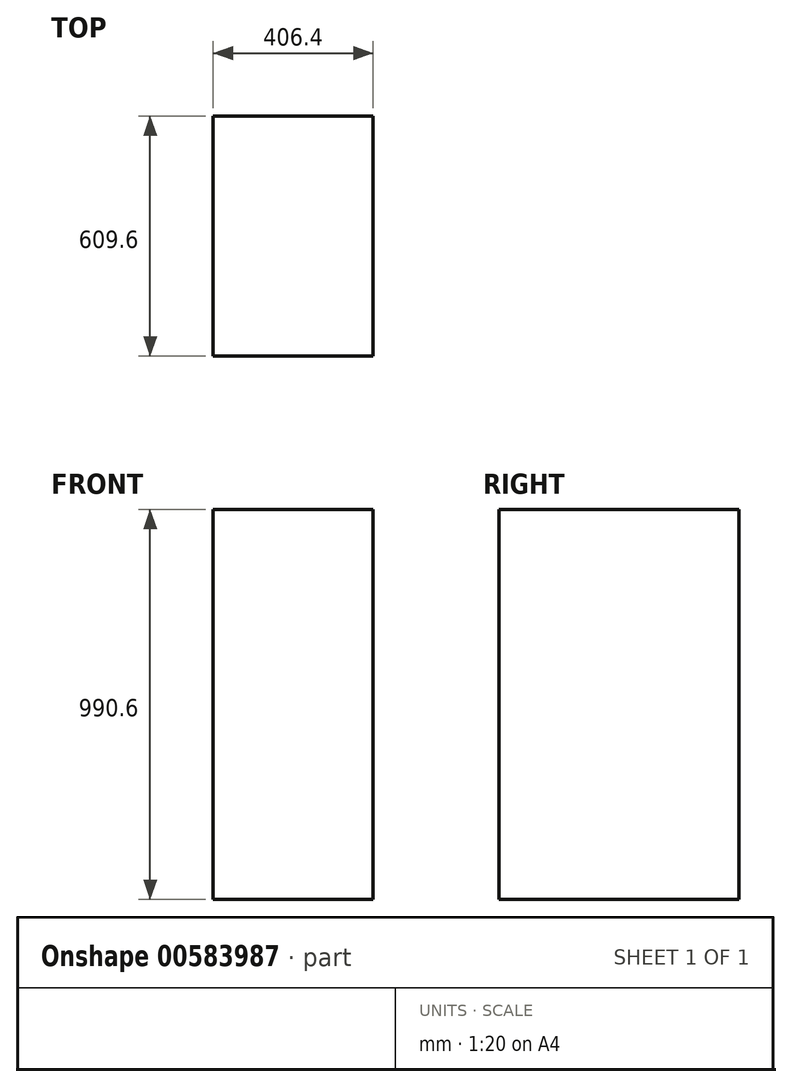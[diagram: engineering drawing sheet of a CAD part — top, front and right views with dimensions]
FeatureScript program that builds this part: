
annotation { "Feature Type Name" : "Feature", "Feature Type Description" : "" }
export const myFeature = defineFeature(function(context is Context, id is Id, definition is map)
    precondition{}
    {
        {
            var Q0;
            Q0=qCreatedBy(makeId("Top.planeOp"),FACE);
            var sketch = newSketch(context, id + "F0", { "sketchPlane" : qUnion([Q0])});
            skLineSegment(sketch, "E0.bottom", {"start": v(-202.1, 475.08) * mm, "end": v(204.3, 475.08) * mm});
            skLineSegment(sketch, "E0.top", {"start": v(-202.1, -134.52) * mm, "end": v(204.3, -134.52) * mm});
            skLineSegment(sketch, "E0.left", {"start": v(-202.1, 475.08) * mm, "end": v(-202.1, -134.52) * mm});
            skLineSegment(sketch, "E0.right", {"start": v(204.3, 475.08) * mm, "end": v(204.3, -134.52) * mm});
            skSolve(sketch);
        }
        {
            var Q0;
            Q0=makeQuery(id+"F0.imprint","IMPRINT",FACE,{"disambiguationData":[TD([[makeQuery(id+"F0.imprint","IMPRINT",EDGE,{"derivedFrom":sQuery(id+"F0.wireOp",EDGE,"E0.bottom")}),-1.0]])]});
            extrude(context, id + "F1", {"entities" : qUnion([Q0]), "depth" : 990.6 * mm, "offsetDistance" : 25.4 * mm});
        }
    });
